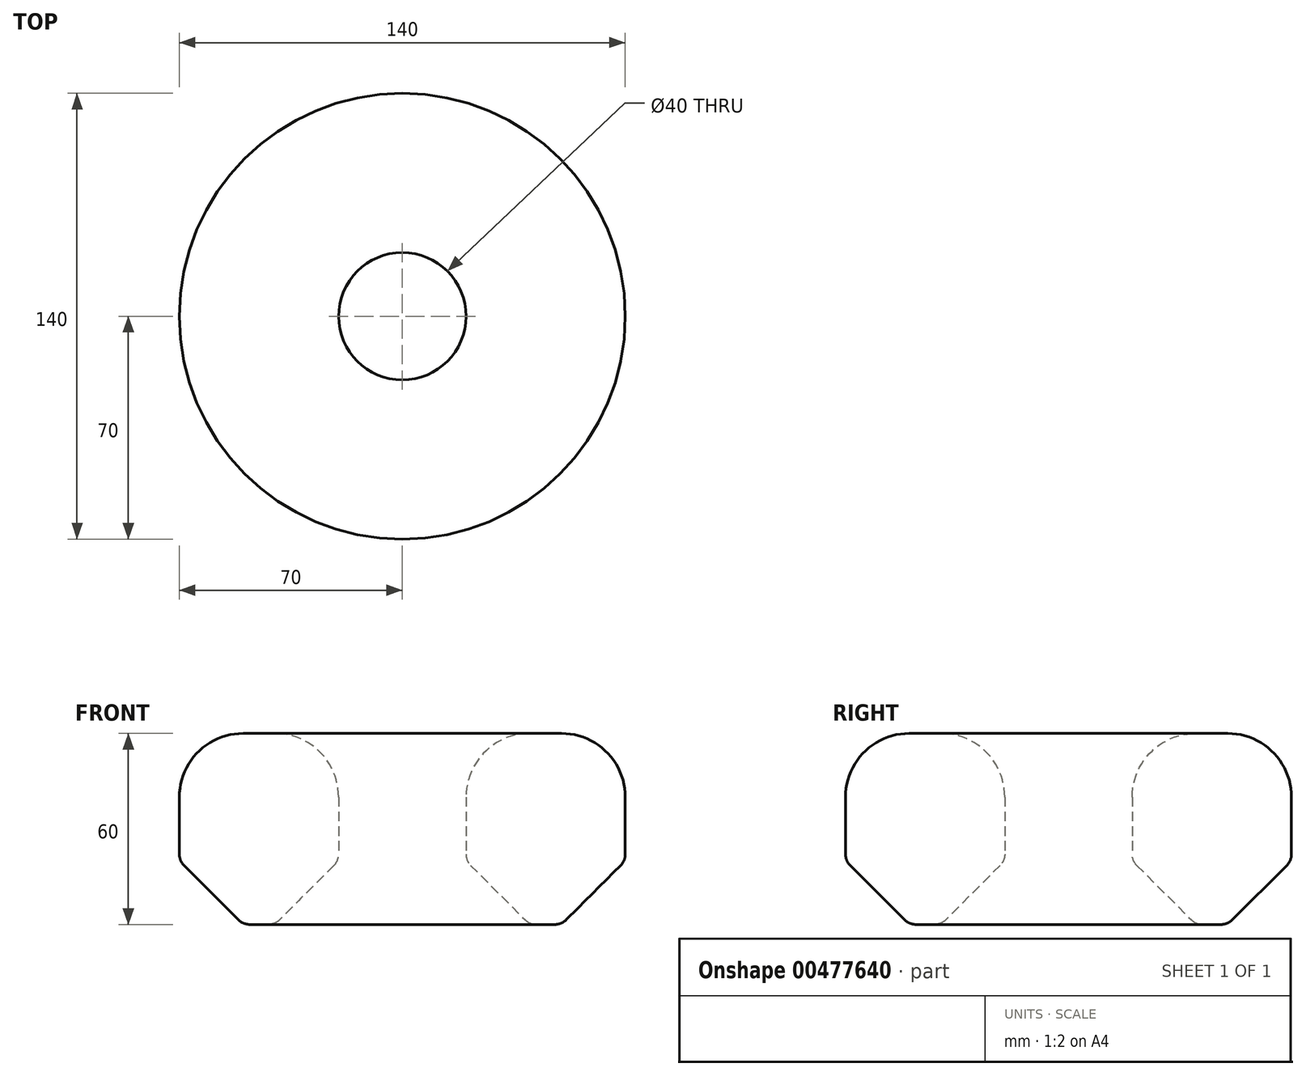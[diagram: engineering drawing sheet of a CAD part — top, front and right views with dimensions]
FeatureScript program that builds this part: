
annotation { "Feature Type Name" : "Feature", "Feature Type Description" : "" }
export const myFeature = defineFeature(function(context is Context, id is Id, definition is map)
    precondition{}
    {
        {
            var Q0;
            Q0=qCreatedBy(makeId("Top.planeOp"),FACE);
            var sketch = newSketch(context, id + "F0", { "sketchPlane" : qUnion([Q0])});
            skCircle(sketch, "E0", {"center": v(0, 0) * mm, "radius": 70 * mm});
            skCircle(sketch, "E1", {"center": v(0, 0) * mm, "radius": 20 * mm});
            skSolve(sketch);
        }
        {
            var Q0;
            Q0=makeQuery(id+"F0.imprint","IMPRINT",FACE,{"disambiguationData":[TD([[makeQuery(id+"F0.imprint","IMPRINT",EDGE,{"derivedFrom":sQuery(id+"F0.wireOp",EDGE,"E0")}),1.0]])]});
            extrude(context, id + "F1", {"entities" : qUnion([Q0]), "depth" : 60 * mm});
        }
        {
            var Q0;
            Q0=makeQuery(id+"F1.opExtrude","CAP_EDGE",EDGE,{"disambiguationData":[OSD([sQuery(id+"F0.wireOp",EDGE,"E0")])],"isStart":false});
            fillet(context, id + "F2", {"entities" : qUnion([Q0]), "radius" : 20 * mm, "tangentPropagation" : true, "allowEdgeOverflow" : false});
        }
        {
            var Q0;
            Q0=makeQuery(id+"F1.opExtrude","CAP_EDGE",EDGE,{"disambiguationData":[OSD([sQuery(id+"F0.wireOp",EDGE,"E0")])],"isStart":true});
            var Q1;
            Q1=makeQuery(id+"F1.opExtrude","CAP_EDGE",EDGE,{"disambiguationData":[OSD([sQuery(id+"F0.wireOp",EDGE,"E1")])],"isStart":true});
            chamfer(context, id + "F3", {"entities" : qUnion([Q0, Q1]), "width" : 20 * mm, "tangentPropagation" : true});
        }
        {
            var Q0;
            Q0=makeQuery(id+"F1.opExtrude","CAP_EDGE",EDGE,{"disambiguationData":[OSD([sQuery(id+"F0.wireOp",EDGE,"E1")])],"isStart":false});
            fillet(context, id + "F4", {"entities" : qUnion([Q0]), "radius" : 20 * mm, "tangentPropagation" : true, "allowEdgeOverflow" : false});
        }
        {
            var Q0;
            {var subQ0=sQuery(id+"F0.wireOp",EDGE,"E0");Q0=makeQuery(id+"F3.opChamfer","BLEND_EDGE",EDGE,{"blendedFrom":[makeQuery(id+"F1.opExtrude","CAP_EDGE",EDGE,{"disambiguationData":[OSD([subQ0])],"isStart":true}),makeQuery(id+"F1.opExtrude","SWEPT_FACE",FACE,{"disambiguationData":[OSD([subQ0])]})],"blendedInto":[makeQuery(id+"F1.opExtrude","SWEPT_FACE",FACE,{"disambiguationData":[OSD([subQ0])]})]});}
            var Q1;
            {var subQ0=sQuery(id+"F0.wireOp",EDGE,"E0");Q1=makeQuery(id+"F3.opChamfer","BLEND_EDGE",EDGE,{"blendedFrom":[makeQuery(id+"F1.opExtrude","CAP_EDGE",EDGE,{"disambiguationData":[OSD([subQ0])],"isStart":true}),makeQuery(id+"F1.opExtrude","CAP_FACE",FACE,{"disambiguationData":[OSD([subQ0,sQuery(id+"F0.wireOp",EDGE,"E1")])],"isStart":true})],"blendedInto":[makeQuery(id+"F1.opExtrude","CAP_FACE",FACE,{"disambiguationData":[OSD([subQ0,sQuery(id+"F0.wireOp",EDGE,"E1")])],"isStart":true})]});}
            var Q2;
            {var subQ0=sQuery(id+"F0.wireOp",EDGE,"E1");Q2=makeQuery(id+"F3.opChamfer","BLEND_EDGE",EDGE,{"blendedFrom":[makeQuery(id+"F1.opExtrude","CAP_EDGE",EDGE,{"disambiguationData":[OSD([subQ0])],"isStart":true}),makeQuery(id+"F1.opExtrude","CAP_FACE",FACE,{"disambiguationData":[OSD([sQuery(id+"F0.wireOp",EDGE,"E0"),subQ0])],"isStart":true})],"blendedInto":[makeQuery(id+"F1.opExtrude","CAP_FACE",FACE,{"disambiguationData":[OSD([sQuery(id+"F0.wireOp",EDGE,"E0"),subQ0])],"isStart":true})]});}
            var Q3;
            {var subQ0=sQuery(id+"F0.wireOp",EDGE,"E1");Q3=makeQuery(id+"F3.opChamfer","BLEND_EDGE",EDGE,{"blendedFrom":[makeQuery(id+"F1.opExtrude","CAP_EDGE",EDGE,{"disambiguationData":[OSD([subQ0])],"isStart":true}),makeQuery(id+"F1.opExtrude","SWEPT_FACE",FACE,{"disambiguationData":[OSD([subQ0])]})],"blendedInto":[makeQuery(id+"F1.opExtrude","SWEPT_FACE",FACE,{"disambiguationData":[OSD([subQ0])]})]});}
            fillet(context, id + "F5", {"entities" : qUnion([Q0, Q1, Q2, Q3]), "radius" : 5 * mm, "tangentPropagation" : true, "allowEdgeOverflow" : false});
        }
    });
